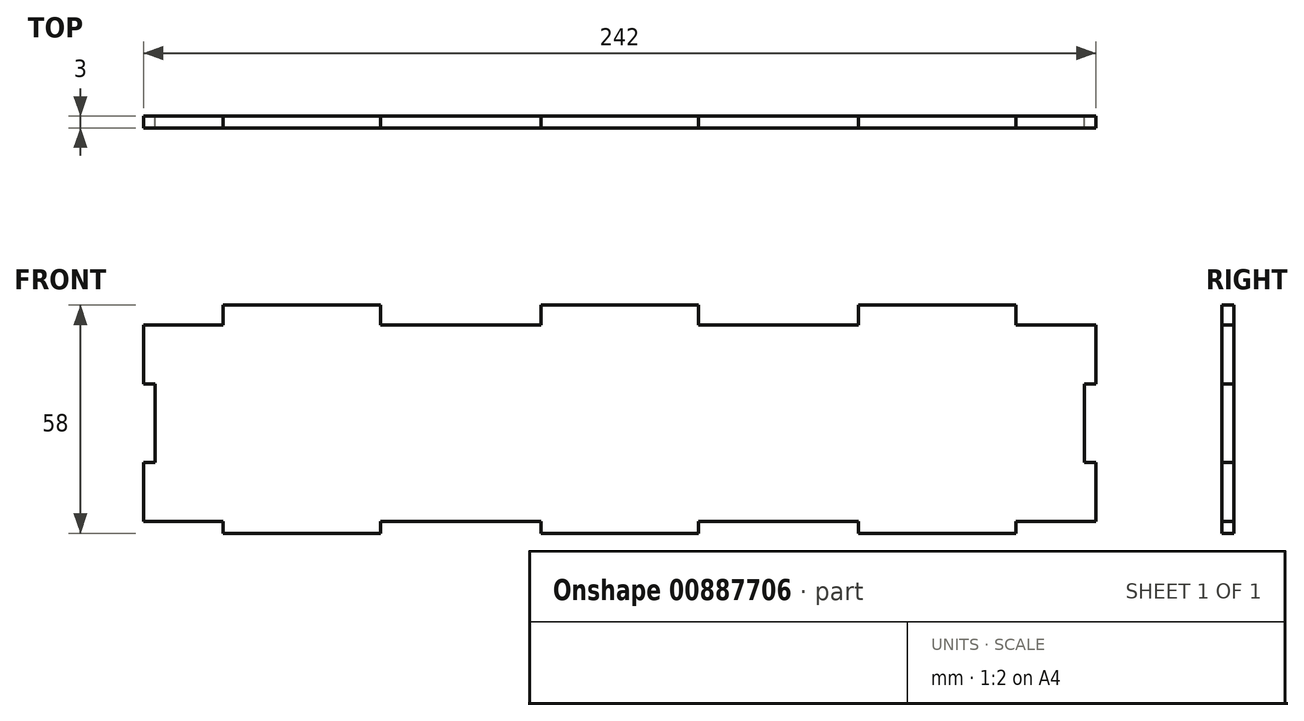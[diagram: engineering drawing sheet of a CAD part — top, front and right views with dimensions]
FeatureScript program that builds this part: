
annotation { "Feature Type Name" : "Feature", "Feature Type Description" : "" }
export const myFeature = defineFeature(function(context is Context, id is Id, definition is map)
    precondition{}
    {
        {
            var Q0;
            Q0=qCreatedBy(makeId("Front.planeOp"),FACE);
            var sketch = newSketch(context, id + "F0", { "sketchPlane" : qUnion([Q0])});
            skLineSegment(sketch, "E0.bottom", {"start": v(121, -25) * mm, "end": v(100.7, -25) * mm});
            skLineSegment(sketch, "E0.top", {"start": v(121, 25) * mm, "end": v(100.7, 25) * mm});
            skLineSegment(sketch, "E0.left", {"start": v(121, -25) * mm, "end": v(121, -10) * mm});
            skLineSegment(sketch, "E0.right", {"start": v(-121, -25) * mm, "end": v(-121, -10) * mm});
            skPoint(sketch, "E0.middle", {"position": v(0, 0) * mm});
            skLineSegment(sketch, "E1", {"start": v(-100.7, -25) * mm, "end": v(-100.7, -28) * mm});
            skLineSegment(sketch, "E2", {"start": v(-100.7, -28) * mm, "end": v(-60.7, -28) * mm});
            skLineSegment(sketch, "E3", {"start": v(-60.7, -28) * mm, "end": v(-60.7, -25) * mm});
            skLineSegment(sketch, "E4", {"start": v(-20, -25) * mm, "end": v(-20, -28) * mm});
            skLineSegment(sketch, "E5", {"start": v(-20, -28) * mm, "end": v(20, -28) * mm});
            skLineSegment(sketch, "E6", {"start": v(20, -28) * mm, "end": v(20, -25) * mm});
            skLineSegment(sketch, "E7.MirrorCS", {"start": v(100.7, -28) * mm, "end": v(60.7, -28) * mm});
            skLineSegment(sketch, "E8.MirrorCS", {"start": v(100.7, -25) * mm, "end": v(100.7, -28) * mm});
            skLineSegment(sketch, "E9.MirrorCS", {"start": v(60.7, -28) * mm, "end": v(60.7, -25) * mm});
            skLineSegment(sketch, "E10.trimOffspring", {"start": v(-100.7, -25) * mm, "end": v(-121, -25) * mm});
            skLineSegment(sketch, "E11.trimOffspring", {"start": v(-20, -25) * mm, "end": v(-60.7, -25) * mm});
            skLineSegment(sketch, "E12.trimOffspring", {"start": v(60.7, -25) * mm, "end": v(20, -25) * mm});
            skLineSegment(sketch, "E13.MirrorCS", {"start": v(-100.7, 25) * mm, "end": v(-100.7, 28) * mm});
            skLineSegment(sketch, "E14.MirrorCS", {"start": v(-60.7, 28) * mm, "end": v(-60.7, 25) * mm});
            skLineSegment(sketch, "E15.MirrorCS", {"start": v(-20, 25) * mm, "end": v(-20, 28) * mm});
            skLineSegment(sketch, "E16.MirrorCS", {"start": v(20, 28) * mm, "end": v(20, 25) * mm});
            skLineSegment(sketch, "E17.MirrorCS", {"start": v(60.7, 28) * mm, "end": v(60.7, 25) * mm});
            skLineSegment(sketch, "E18.MirrorCS", {"start": v(100.7, 25) * mm, "end": v(100.7, 28) * mm});
            skLineSegment(sketch, "E19.trimOffspring", {"start": v(-100.7, 25) * mm, "end": v(-121, 25) * mm});
            skLineSegment(sketch, "E20.trimOffspring", {"start": v(-20, 25) * mm, "end": v(-60.7, 25) * mm});
            skLineSegment(sketch, "E21.trimOffspring", {"start": v(60.7, 25) * mm, "end": v(20, 25) * mm});
            skLineSegment(sketch, "E22", {"start": v(-121, 10) * mm, "end": v(-118, 10) * mm});
            skLineSegment(sketch, "E23", {"start": v(-118, 10) * mm, "end": v(-118, -10) * mm});
            skLineSegment(sketch, "E24", {"start": v(-118, -10) * mm, "end": v(-121, -10) * mm});
            skLineSegment(sketch, "E25.trimOffspring", {"start": v(-121, 10) * mm, "end": v(-121, 25) * mm});
            skLineSegment(sketch, "E26.MirrorCS", {"start": v(118, 10) * mm, "end": v(118, -10) * mm});
            skLineSegment(sketch, "E27.MirrorCS", {"start": v(121, 10) * mm, "end": v(118, 10) * mm});
            skLineSegment(sketch, "E28.MirrorCS", {"start": v(118, -10) * mm, "end": v(121, -10) * mm});
            skLineSegment(sketch, "E29.trimOffspring", {"start": v(121, 10) * mm, "end": v(121, 25) * mm});
            skLineSegment(sketch, "E30", {"start": v(-100.7, 28) * mm, "end": v(-100.7, 30) * mm});
            skLineSegment(sketch, "E31", {"start": v(-100.7, 30) * mm, "end": v(-60.7, 30) * mm});
            skLineSegment(sketch, "E32", {"start": v(-60.7, 30) * mm, "end": v(-60.7, 28) * mm});
            skPoint(sketch, "E33.MirrorCS.start.orphan", {"position": v(-100.7, 28) * mm});
            skLineSegment(sketch, "E34.MirrorCS", {"start": v(100.7, 30) * mm, "end": v(60.7, 30) * mm});
            skLineSegment(sketch, "E35.MirrorCS", {"start": v(60.7, 30) * mm, "end": v(60.7, 28) * mm});
            skLineSegment(sketch, "E36.MirrorCS", {"start": v(100.7, 28) * mm, "end": v(100.7, 30) * mm});
            skPoint(sketch, "E37.MirrorCS.end.orphan", {"position": v(60.7, 28) * mm});
            skPoint(sketch, "E37.MirrorCS.start.orphan", {"position": v(100.7, 28) * mm});
            skLineSegment(sketch, "E38", {"start": v(-20, 28) * mm, "end": v(-20, 30) * mm});
            skLineSegment(sketch, "E39", {"start": v(-20, 30) * mm, "end": v(20, 30) * mm});
            skLineSegment(sketch, "E40", {"start": v(20, 30) * mm, "end": v(20, 28) * mm});
            skPoint(sketch, "E41.MirrorCS.start.orphan", {"position": v(-20, 28) * mm});
            skSolve(sketch);
        }
        {
            var Q0;
            Q0 = qSketchRegion(id + "F0", true);
            extrude(context, id + "F1", {"entities" : qUnion([Q0]), "depth" : 3 * mm, "offsetDistance" : 25 * mm});
        }
    });
